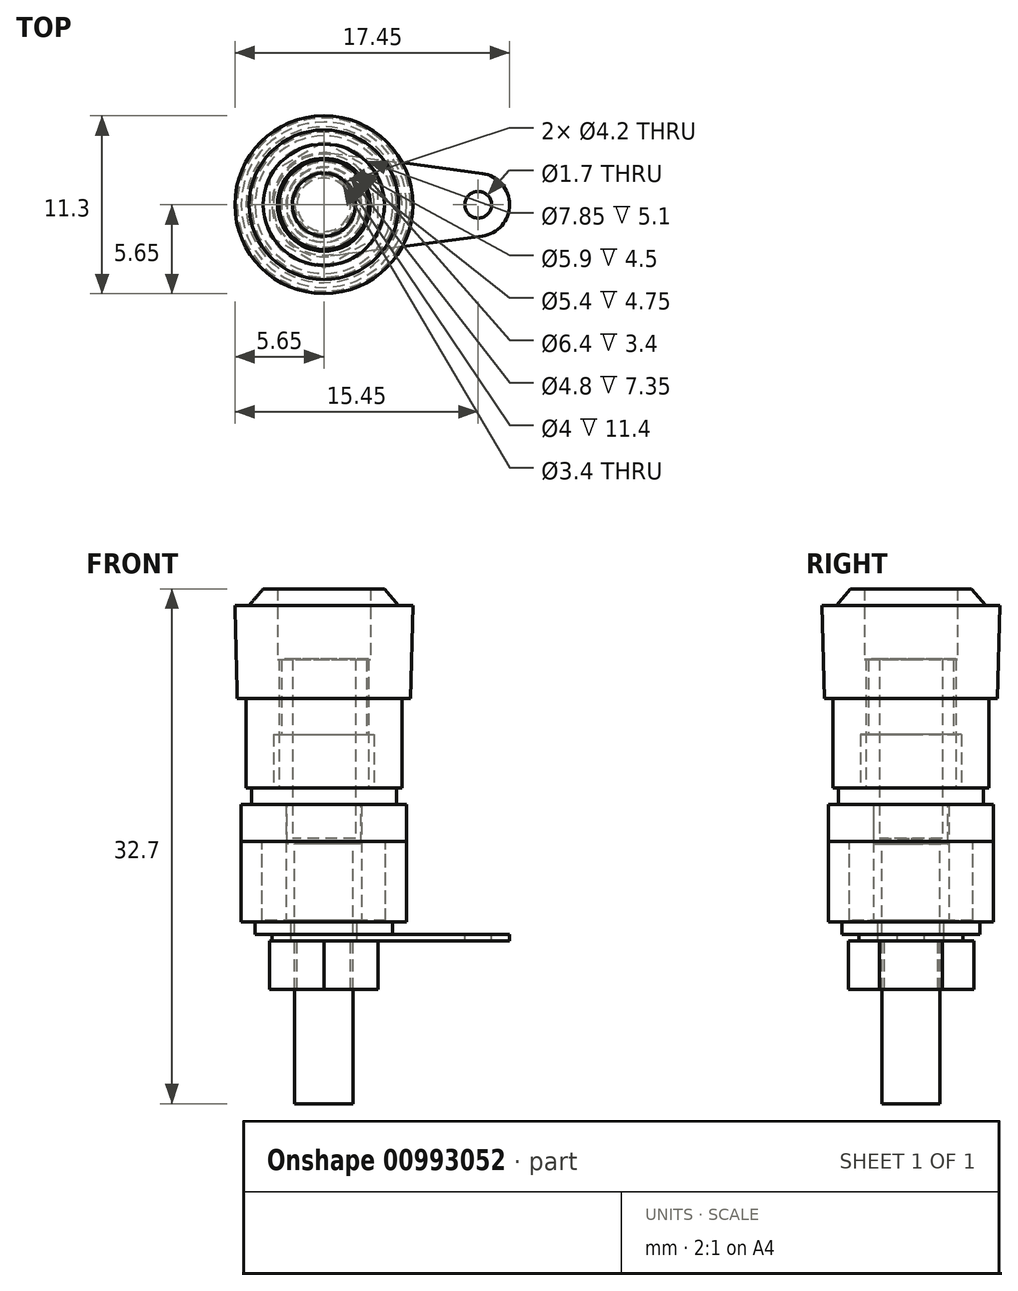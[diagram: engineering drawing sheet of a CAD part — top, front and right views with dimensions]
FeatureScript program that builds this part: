
annotation { "Feature Type Name" : "Feature", "Feature Type Description" : "" }
export const myFeature = defineFeature(function(context is Context, id is Id, definition is map)
    precondition{}
    {
        {
            var Q0;
            Q0=qCreatedBy(makeId("Top.planeOp"),FACE);
            var sketch = newSketch(context, id + "F0", { "sketchPlane" : qUnion([Q0])});
            skCircle(sketch, "E0", {"center": v(0, 0) * mm, "radius": 2.4 * mm});
            skCircle(sketch, "E1", {"center": v(0, 0) * mm, "radius": 3.92 * mm});
            skCircle(sketch, "E2", {"center": v(0, 0) * mm, "radius": 5.25 * mm});
            skSolve(sketch);
        }
        {
            var Q0;
            Q0=makeQuery(id+"F0.imprint","IMPRINT",FACE,{"disambiguationData":[TD([[makeQuery(id+"F0.imprint","IMPRINT",EDGE,{"derivedFrom":sQuery(id+"F0.wireOp",EDGE,"E1")}),-1.0]])]});
            var Q1;
            Q1=makeQuery(id+"F0.imprint","IMPRINT",FACE,{"disambiguationData":[TD([[makeQuery(id+"F0.imprint","IMPRINT",EDGE,{"derivedFrom":sQuery(id+"F0.wireOp",EDGE,"E0")}),-1.0]])]});
            extrude(context, id + "F1", {"entities" : qUnion([Q0, Q1]), "depth" : 2.35 * mm, "offsetDistance" : 25.4 * mm});
        }
        {
            var Q0;
            Q0=makeQuery(id+"F0.imprint","IMPRINT",FACE,{"disambiguationData":[TD([[makeQuery(id+"F0.imprint","IMPRINT",EDGE,{"derivedFrom":sQuery(id+"F0.wireOp",EDGE,"E0")}),-1.0]])]});
            extrude(context, id + "F2", {"entities" : qUnion([Q0]), "operationType" : NewBodyOperationType.ADD, "oppositeDirection" : true, "depth" : 5 * mm, "offsetDistance" : 25.4 * mm});
        }
        {
            var Q0;
            Q0=makeQuery(id+"F0.imprint","IMPRINT",FACE,{"disambiguationData":[TD([[makeQuery(id+"F0.imprint","IMPRINT",EDGE,{"derivedFrom":sQuery(id+"F0.wireOp",EDGE,"E1")}),-1.0]])]});
            extrude(context, id + "F3", {"entities" : qUnion([Q0]), "oppositeDirection" : true, "depth" : 5.1 * mm, "offsetDistance" : 25 * mm});
        }
        {
            var Q0;
            Q0=makeQuery(id+"F1.opExtrude","CAP_FACE",FACE,{"disambiguationData":[OSD([sQuery(id+"F0.wireOp",EDGE,"E0"),sQuery(id+"F0.wireOp",EDGE,"E2")])],"isStart":false});
            var sketch = newSketch(context, id + "F4", { "sketchPlane" : qUnion([Q0])});
            skCircle(sketch, "E3", {"center": v(0, 0) * mm, "radius": 2.35 * mm});
            skCircle(sketch, "E4", {"center": v(0, 0) * mm, "radius": 4.6 * mm});
            skCircle(sketch, "E5", {"center": v(0, 0) * mm, "radius": 2.85 * mm});
            skCircle(sketch, "E6", {"center": v(0, 0) * mm, "radius": 1.85 * mm});
            skCircle(sketch, "E7", {"center": v(0, 0) * mm, "radius": 2 * mm});
            skSolve(sketch);
        }
        {
            var Q0;
            Q0=makeQuery(id+"F4.imprint","IMPRINT",FACE,{"disambiguationData":[TD([[makeQuery(id+"F4.imprint","IMPRINT",EDGE,{"derivedFrom":sQuery(id+"F4.wireOp",EDGE,"E4")}),1.0]])]});
            var Q1;
            Q1=makeQuery(id+"F4.imprint","IMPRINT",FACE,{"disambiguationData":[TD([[makeQuery(id+"F4.imprint","IMPRINT",EDGE,{"derivedFrom":sQuery(id+"F4.wireOp",EDGE,"E5")}),1.0]])]});
            var Q2;
            Q2=makeQuery(id+"F4.imprint","IMPRINT",FACE,{"disambiguationData":[TD([[makeQuery(id+"F4.imprint","IMPRINT",EDGE,{"derivedFrom":sQuery(id+"F4.wireOp",EDGE,"E3")}),1.0]])]});
            var Q3;
            Q3=makeQuery(id+"F4.imprint","IMPRINT",FACE,{"disambiguationData":[TD([[makeQuery(id+"F4.imprint","IMPRINT",EDGE,{"derivedFrom":sQuery(id+"F4.wireOp",EDGE,"E3")}),-1.0]])]});
            extrude(context, id + "F5", {"entities" : qUnion([Q0, Q1, Q2, Q3]), "depth" : 1.05 * mm, "offsetDistance" : 25 * mm});
        }
        {
            var Q0;
            Q0=makeQuery(id+"F4.imprint","IMPRINT",FACE,{"disambiguationData":[TD([[makeQuery(id+"F4.imprint","IMPRINT",EDGE,{"derivedFrom":sQuery(id+"F4.wireOp",EDGE,"E3")}),1.0]])]});
            var Q1;
            Q1=makeQuery(id+"F4.imprint","IMPRINT",FACE,{"disambiguationData":[TD([[makeQuery(id+"F4.imprint","IMPRINT",EDGE,{"derivedFrom":sQuery(id+"F4.wireOp",EDGE,"E3")}),-1.0]])]});
            var Q2;
            Q2=makeQuery(id+"F4.imprint","IMPRINT",FACE,{"disambiguationData":[TD([[makeQuery(id+"F4.imprint","IMPRINT",EDGE,{"derivedFrom":sQuery(id+"F4.wireOp",EDGE,"E5")}),1.0]])]});
            extrude(context, id + "F6", {"entities" : qUnion([Q0, Q1, Q2]), "operationType" : NewBodyOperationType.ADD, "depth" : (1.05 + 8.2) * mm, "offsetDistance" : 25 * mm});
        }
        {
            var Q0;
            Q0=makeQuery(id+"F4.imprint","IMPRINT",FACE,{"disambiguationData":[TD([[makeQuery(id+"F4.imprint","IMPRINT",EDGE,{"derivedFrom":sQuery(id+"F4.wireOp",EDGE,"E3")}),1.0]])]});
            var Q1;
            Q1=makeQuery(id+"F4.imprint","IMPRINT",FACE,{"disambiguationData":[TD([[makeQuery(id+"F4.imprint","IMPRINT",EDGE,{"derivedFrom":sQuery(id+"F4.wireOp",EDGE,"E6")}),-1.0]])]});
            extrude(context, id + "F7", {"entities" : qUnion([Q0, Q1]), "operationType" : NewBodyOperationType.ADD, "oppositeDirection" : true, "depth" : 2.5 * mm, "offsetDistance" : 25 * mm});
        }
        {
            var Q0;
            Q0=makeQuery(id+"F4.imprint","IMPRINT",FACE,{"disambiguationData":[TD([[makeQuery(id+"F4.imprint","IMPRINT",EDGE,{"derivedFrom":sQuery(id+"F4.wireOp",EDGE,"E6")}),1.0]])]});
            extrude(context, id + "F8", {"entities" : qUnion([Q0]), "operationType" : NewBodyOperationType.ADD, "oppositeDirection" : true, "depth" : 19 * mm, "offsetDistance" : 25 * mm});
        }
        {
            var Q0;
            Q0=makeQuery(id+"F4.imprint","IMPRINT",FACE,{"disambiguationData":[TD([[makeQuery(id+"F4.imprint","IMPRINT",EDGE,{"derivedFrom":sQuery(id+"F4.wireOp",EDGE,"E6")}),1.0]])]});
            var Q1;
            Q1=makeQuery(id+"F4.imprint","IMPRINT",FACE,{"disambiguationData":[TD([[makeQuery(id+"F4.imprint","IMPRINT",EDGE,{"derivedFrom":sQuery(id+"F4.wireOp",EDGE,"E6")}),-1.0]])]});
            extrude(context, id + "F9", {"entities" : qUnion([Q0, Q1]), "operationType" : NewBodyOperationType.REMOVE, "oppositeDirection" : true, "depth" : (11.4 - (1.05 + 8.2)) * mm, "offsetDistance" : 25 * mm});
        }
        {
            var Q0;
            Q0=qCreatedBy(makeId("Front.planeOp"),FACE);
            var sketch = newSketch(context, id + "F10", { "sketchPlane" : qUnion([Q0])});
            skLineSegment(sketch, "E8", {"start": v(2.95, 16.05) * mm, "end": v(3.85, 16.05) * mm});
            skLineSegment(sketch, "E9", {"start": v(3.85, 16.05) * mm, "end": v(4.75, 15) * mm});
            skLineSegment(sketch, "E10", {"start": v(4.75, 15) * mm, "end": v(5.65, 15) * mm});
            skLineSegment(sketch, "E11", {"start": v(5.65, 15) * mm, "end": v(5.5, 9.1) * mm});
            skLineSegment(sketch, "E12", {"start": v(5.5, 9.1) * mm, "end": v(4.95, 9.1) * mm});
            skLineSegment(sketch, "E13", {"start": v(4.95, 9.1) * mm, "end": v(4.95, 3.4) * mm});
            skLineSegment(sketch, "E14", {"start": v(4.95, 3.4) * mm, "end": v(3.2, 3.4) * mm});
            skLineSegment(sketch, "E15", {"start": v(3.2, 3.4) * mm, "end": v(3.2, 6.8) * mm});
            skLineSegment(sketch, "E16", {"start": v(3.2, 6.8) * mm, "end": v(2.7, 6.8) * mm});
            skLineSegment(sketch, "E17", {"start": v(2.7, 6.8) * mm, "end": v(2.7, 11.55) * mm});
            skLineSegment(sketch, "E18", {"start": v(2.7, 11.55) * mm, "end": v(2.95, 11.55) * mm});
            skLineSegment(sketch, "E19", {"start": v(2.95, 11.55) * mm, "end": v(2.95, 16.05) * mm});
            skLineSegment(sketch, "E20", {"start": v(0, 0) * mm, "end": v(0, 25.23) * mm, "construction": true});
            skSolve(sketch);
        }
        {
            var Q0;
            Q0=makeQuery(id+"F10.imprint","IMPRINT",FACE,{"disambiguationData":[TD([[makeQuery(id+"F10.imprint","IMPRINT",EDGE,{"derivedFrom":sQuery(id+"F10.wireOp",EDGE,"E8")}),-1.0]])]});
            var Q1;
            Q1=sQuery(id+"F10.wireOp",EDGE,"E20");
            revolve(context, id + "F11", {"surfaceOperationType" : NewSurfaceOperationType.NEW, "entities" : qUnion([Q0]), "axis" : qUnion([Q1]), "revolveType" : RevolveType.FULL});
        }
        {
            var Q0;
            Q0=makeQuery(id+"F3.opExtrude","CAP_FACE",FACE,{"disambiguationData":[OSD([sQuery(id+"F0.wireOp",EDGE,"E1"),sQuery(id+"F0.wireOp",EDGE,"E2")])],"isStart":false});
            var sketch = newSketch(context, id + "F12", { "sketchPlane" : qUnion([Q0])});
            skCircle(sketch, "E21", {"center": v(0, 0) * mm, "radius": 2.1 * mm});
            skCircle(sketch, "E22", {"center": v(0, 0) * mm, "radius": 4.38 * mm});
            skSolve(sketch);
        }
        {
            var Q0;
            Q0=makeQuery(id+"F12.imprint","IMPRINT",FACE,{"disambiguationData":[TD([[makeQuery(id+"F12.imprint","IMPRINT",EDGE,{"derivedFrom":sQuery(id+"F12.wireOp",EDGE,"E21")}),-1.0]])]});
            var Q1;
            Q1=makeQuery(id+"F12.imprint","IMPRINT",FACE,{"disambiguationData":[TD([[makeQuery(id+"F12.imprint","IMPRINT",EDGE,{"derivedFrom":sQuery(id+"F12.wireOp",EDGE,"E22")}),1.0]])]});
            extrude(context, id + "F13", {"entities" : qUnion([Q0, Q1]), "depth" : 0.8 * mm, "offsetDistance" : 25 * mm});
        }
        {
            var Q0;
            Q0=makeQuery(id+"F13.opExtrude","CAP_FACE",FACE,{"disambiguationData":[OSD([sQuery(id+"F12.wireOp",EDGE,"E21"),sQuery(id+"F12.wireOp",EDGE,"E22")])],"isStart":false});
            var sketch = newSketch(context, id + "F14", { "sketchPlane" : qUnion([Q0])});
            skCircle(sketch, "E23", {"center": v(0, 0) * mm, "radius": 1.95 * mm});
            skCircle(sketch, "E24", {"center": v(9.8, 0) * mm, "radius": 0.85 * mm});
            skArc(sketch, "E25", {"start": v(10.07, -1.98) * mm, "mid": v(11.8, 0) * mm, "end": v(10.07, 1.98) * mm});
            skArc(sketch, "E26", {"start": v(0.44, 3.27) * mm, "mid": v(-3.3, 0) * mm, "end": v(0.44, -3.27) * mm});
            skLineSegment(sketch, "E27", {"start": v(0.44, -3.27) * mm, "end": v(10.07, -1.98) * mm});
            skLineSegment(sketch, "E28", {"start": v(10.07, 1.98) * mm, "end": v(0.44, 3.27) * mm});
            skSolve(sketch);
        }
        {
            var Q0;
            {var subQ1=sQuery(id+"F14.wireOp",EDGE,"E26");Q0=makeQuery(id+"F14.imprint","IMPRINT",FACE,{"disambiguationData":[TD([[makeQuery(id+"F14.imprint","IMPRINT",EDGE,{"derivedFrom":subQ1}),1.0]])]});}
            var Q1;
            Q1=makeQuery(id+"F14.imprint","IMPRINT",FACE,{"disambiguationData":[TD([[makeQuery(id+"F14.imprint","IMPRINT",EDGE,{"derivedFrom":sQuery(id+"F14.wireOp",EDGE,"E24")}),-1.0]])]});
            extrude(context, id + "F15", {"entities" : qUnion([Q0, Q1]), "depth" : 0.4 * mm, "offsetDistance" : 25 * mm});
        }
        {
            var Q0;
            Q0=makeQuery(id+"F15.opExtrude","CAP_FACE",FACE,{"disambiguationData":[OSD([sQuery(id+"F12.wireOp",EDGE,"E21"),sQuery(id+"F14.wireOp",EDGE,"E24"),sQuery(id+"F14.wireOp",EDGE,"E25"),sQuery(id+"F14.wireOp",EDGE,"E26"),sQuery(id+"F14.wireOp",EDGE,"E27"),sQuery(id+"F14.wireOp",EDGE,"E28")])],"isStart":false});
            var sketch = newSketch(context, id + "F16", { "sketchPlane" : qUnion([Q0])});
            skCircle(sketch, "E29", {"center": v(0, 0) * mm, "radius": 3.98 * mm, "construction": true});
            skLineSegment(sketch, "E30", {"start": v(0, 3.98) * mm, "end": v(3.45, 2) * mm});
            skLineSegment(sketch, "E31", {"start": v(3.45, 2) * mm, "end": v(3.45, -2) * mm});
            skLineSegment(sketch, "E32", {"start": v(3.45, -2) * mm, "end": v(0, -3.98) * mm});
            skLineSegment(sketch, "E33", {"start": v(0, -3.98) * mm, "end": v(-3.45, -2) * mm});
            skLineSegment(sketch, "E34", {"start": v(-3.45, -2) * mm, "end": v(-3.45, 2) * mm});
            skLineSegment(sketch, "E35", {"start": v(-3.45, 2) * mm, "end": v(0, 3.98) * mm});
            skCircle(sketch, "E36", {"center": v(0, 0) * mm, "radius": 1.7 * mm});
            skSolve(sketch);
        }
        {
            var Q0;
            Q0=makeQuery(id+"F16.imprint","IMPRINT",FACE,{"disambiguationData":[TD([[makeQuery(id+"F16.imprint","IMPRINT",EDGE,{"derivedFrom":sQuery(id+"F16.wireOp",EDGE,"E36")}),-1.0]])]});
            var Q1;
            {var subQ0=sQuery(id+"F16.wireOp",EDGE,"E33");Q1=makeQuery(id+"F16.imprint","IMPRINT",FACE,{"disambiguationData":[TD([[makeQuery(id+"F16.imprint","IMPRINT",EDGE,{"derivedFrom":subQ0}),-1.0]])]});}
            var Q2;
            {var subQ1=sQuery(id+"F16.wireOp",EDGE,"E31");Q2=makeQuery(id+"F16.imprint","IMPRINT",FACE,{"disambiguationData":[TD([[makeQuery(id+"F16.imprint","IMPRINT",EDGE,{"derivedFrom":subQ1}),-1.0]])]});}
            extrude(context, id + "F17", {"entities" : qUnion([Q0, Q1, Q2]), "depth" : 3.1 * mm, "offsetDistance" : 25 * mm});
        }
    });
